# Revit family: Шаровой кран с маховиком бабочка 2100
name_source: partatom
category: Rohrzubehör
units: mm (PartAtom-declared; Revit-internal decimal feet)

## family parameters
Arbeitsebenenbasiert = Nein
Beim Laden mit Abzugskörper schneiden = Nein
Bemaßung runder Anschluss = Durchmesser verwenden
Gemeinsam genutzt = Nein
Immer vertikal = Ja
OmniClass-Nummer = 23.65.55.14
OmniClass-Titel = Valves for Liquid Services
Teiletyp = Unterbricht

## types (1)
- Шаровой кран с маховиком бабочка 2100
    Hersteller = HERZ Armaturen Ges.m.b.H
    SCTWCODE = 04;04:02
    SCTWSEQ = FW;SBT_TYP_FW="103";2
    URL = www.herz-armaturen.ru
    Vorgabe-Ansicht = 0 mm  [stored 0 ft]
    W01 = 135.00°
    Корпус = штампованная латунь, устойчивая к селективной цинковой коррозии, согласно EN 12420
    Макс. рабочая температура = 85 °C
    Макс. рабочее давление = 2500000.0 Pa
    Область применения = Шаровой кран используется в качестве запорной арматуры.
Область применения - система питьевого водоснабжения.
Рабочие параметры (температура и давление) должны соблюдаться.
    Примечание = В соответствии со статьей 33 Регламента REACH (Registration; Evaluation; Authorisation; Restriction of Chemicals) (EC № 1907/2006) мы обязаны указать, что свинец внесен в список SVHC (Substances of Very High Concern - вещества очень высокой важности) и весовой процент свинца во всех латунных компонентах заводского изготовления в наших изделиях, превышает 0,1 % (w/w) (CAS: 7439-92-1 / EINECS: 231-100-4).
Поскольку свинец является легирующим компонентом сплава, прямое негативное влияние исключается, и поэтому дополнительной информации о безопасном использовании не требуется.
    Резьба = согласно  ISO 228
    Рукоятка = алюминий, окрашен в зеленый цвет
    Среда = Питьевая вода
    Уплотнение шара = PTFE
    Уплотнение шпинделя = EPDM 70 ShA
    Шар = штампованная латунь, хромированный полнопроходной шар

note: [stored X ft] marks values corroborated as IEEE doubles in the binary element streams (Revit-internal decimal feet)
